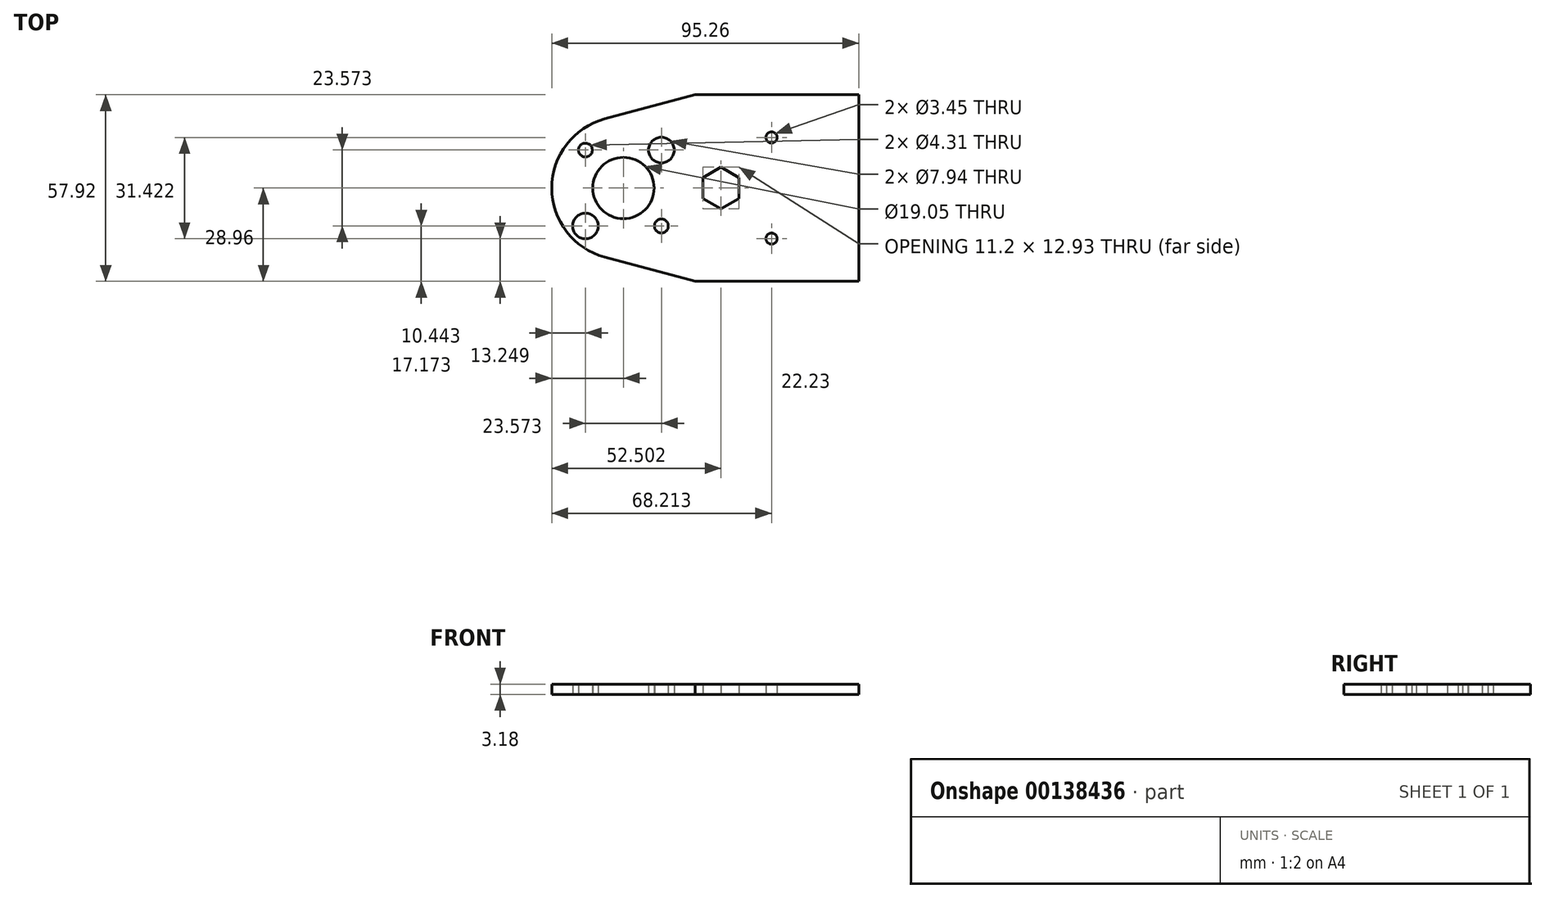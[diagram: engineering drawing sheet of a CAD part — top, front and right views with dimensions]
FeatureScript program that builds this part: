
annotation { "Feature Type Name" : "Feature", "Feature Type Description" : "" }
export const myFeature = defineFeature(function(context is Context, id is Id, definition is map)
    precondition{}
    {
        {
            var Q0;
            Q0=qCreatedBy(makeId("Top.planeOp"),FACE);
            var sketch = newSketch(context, id + "F0", { "sketchPlane" : qUnion([Q0])});
            skCircle(sketch, "E0", {"center": v(0, 0) * mm, "radius": 9.53 * mm});
            skLineSegment(sketch, "E1.bottom", {"start": v(-11.79, 11.79) * mm, "end": v(11.79, 11.79) * mm, "construction": true});
            skLineSegment(sketch, "E1.top", {"start": v(-11.79, -11.79) * mm, "end": v(11.79, -11.79) * mm, "construction": true});
            skLineSegment(sketch, "E1.left", {"start": v(-11.79, 11.79) * mm, "end": v(-11.79, -11.79) * mm, "construction": true});
            skLineSegment(sketch, "E1.right", {"start": v(11.79, 11.79) * mm, "end": v(11.79, -11.79) * mm, "construction": true});
            skCircle(sketch, "E2", {"center": v(0, 0) * mm, "radius": 11.11 * mm, "construction": true});
            skCircle(sketch, "E3", {"center": v(-11.79, 11.79) * mm, "radius": 5.56 * mm, "construction": true});
            skCircle(sketch, "E4", {"center": v(-11.79, 11.79) * mm, "radius": 2.15 * mm});
            skCircle(sketch, "E5", {"center": v(11.79, 11.79) * mm, "radius": 3.97 * mm});
            skCircle(sketch, "E6", {"center": v(-11.79, -11.79) * mm, "radius": 3.97 * mm});
            skCircle(sketch, "E7", {"center": v(11.79, -11.79) * mm, "radius": 2.15 * mm});
            skLineSegment(sketch, "E8", {"start": v(0, 0) * mm, "end": v(22.23, 0) * mm, "construction": true});
            skLineSegment(sketch, "E9.bottom", {"start": v(22.23, 28.96) * mm, "end": v(73.03, 28.96) * mm});
            skLineSegment(sketch, "E9.top", {"start": v(22.23, -28.96) * mm, "end": v(73.03, -28.96) * mm});
            skLineSegment(sketch, "E9.left", {"start": v(22.23, 28.96) * mm, "end": v(22.23, -28.96) * mm, "construction": true});
            skLineSegment(sketch, "E9.right", {"start": v(73.03, 28.96) * mm, "end": v(73.03, -28.96) * mm});
            skArc(sketch, "E10", {"start": v(-5.75, 21.47) * mm, "mid": v(-22.22, 0) * mm, "end": v(-5.75, -21.47) * mm});
            skLineSegment(sketch, "E11", {"start": v(-5.75, 21.47) * mm, "end": v(22.23, 28.96) * mm});
            skLineSegment(sketch, "E12", {"start": v(-5.75, -21.47) * mm, "end": v(22.23, -28.96) * mm});
            skLineSegment(sketch, "E13", {"start": v(-5.75, 21.47) * mm, "end": v(8.24, 21.47) * mm, "construction": true});
            skLineSegment(sketch, "E14", {"start": v(8.24, 21.47) * mm, "end": v(8.24, 25.22) * mm, "construction": true});
            skLineSegment(sketch, "E15", {"start": v(22.23, 0) * mm, "end": v(30.27, 0) * mm, "construction": true});
            skCircle(sketch, "E16.cCircle", {"center": v(30.27, 0) * mm, "radius": 5.6 * mm, "construction": true});
            skLineSegment(sketch, "E16.0", {"start": v(35.87, 3.23) * mm, "end": v(35.87, -3.23) * mm});
            skLineSegment(sketch, "E16.1", {"start": v(35.87, -3.23) * mm, "end": v(30.27, -6.47) * mm});
            skLineSegment(sketch, "E16.2", {"start": v(30.27, -6.47) * mm, "end": v(24.67, -3.23) * mm});
            skLineSegment(sketch, "E16.3", {"start": v(24.67, -3.23) * mm, "end": v(24.67, 3.23) * mm});
            skLineSegment(sketch, "E16.4", {"start": v(24.67, 3.23) * mm, "end": v(30.27, 6.47) * mm});
            skLineSegment(sketch, "E16.5", {"start": v(30.27, 6.47) * mm, "end": v(35.87, 3.23) * mm});
            skPoint(sketch, "E16.0.midPoint", {"position": v(35.87, 0) * mm});
            skLineSegment(sketch, "E17", {"start": v(30.27, 0) * mm, "end": v(45.98, 0) * mm, "construction": true});
            skLineSegment(sketch, "E18", {"start": v(45.98, 15.71) * mm, "end": v(45.98, -15.71) * mm, "construction": true});
            skLineSegment(sketch, "E19", {"start": v(45.98, 15.71) * mm, "end": v(30.27, 0) * mm, "construction": true});
            skCircle(sketch, "E20", {"center": v(45.98, 15.71) * mm, "radius": 1.73 * mm});
            skCircle(sketch, "E21", {"center": v(45.98, -15.71) * mm, "radius": 1.73 * mm});
            skSolve(sketch);
        }
        {
            var Q0;
            Q0=qSketchRegion(id+"F0",true);
            extrude(context, id + "F1", {"entities" : qUnion([Q0]), "depth" : 3.17 * mm});
        }
    });
